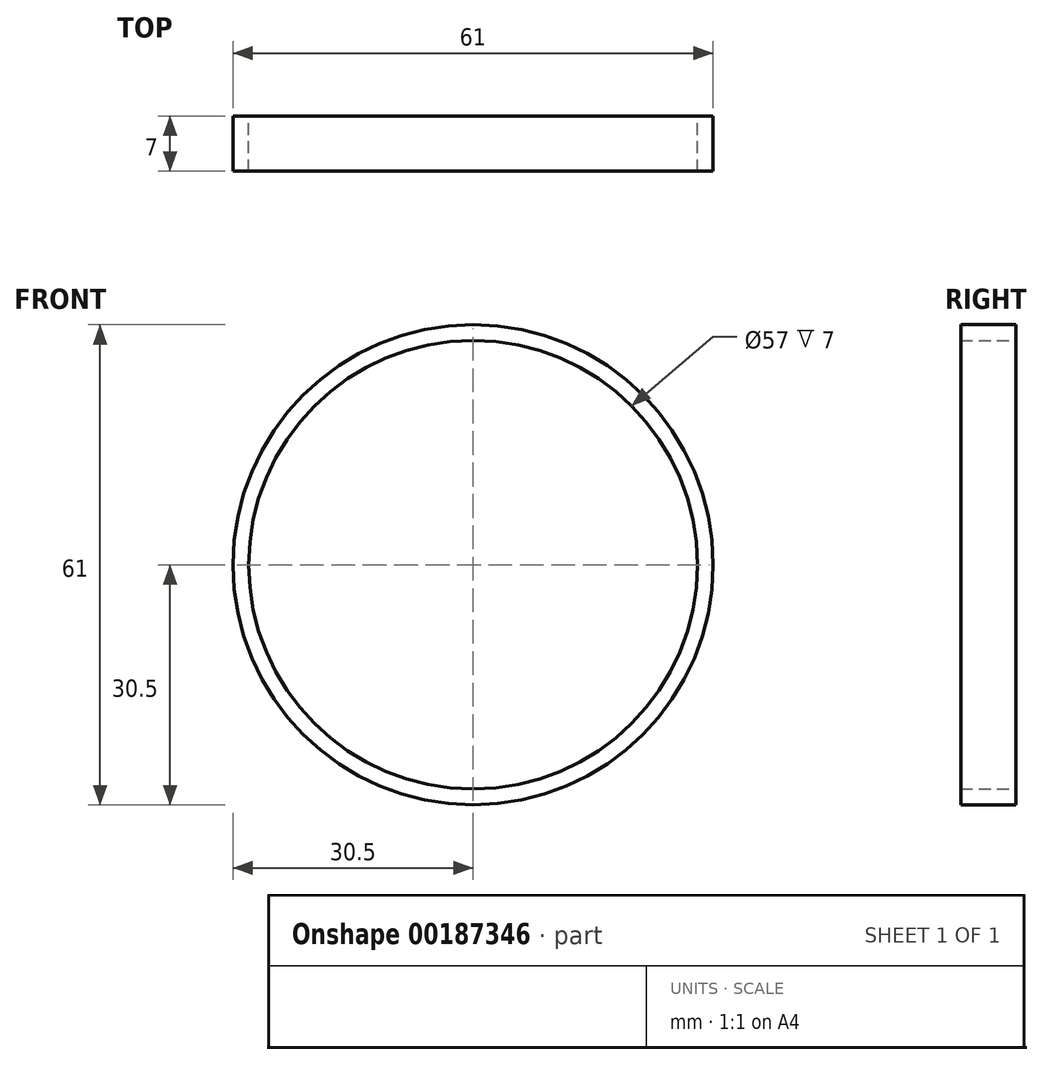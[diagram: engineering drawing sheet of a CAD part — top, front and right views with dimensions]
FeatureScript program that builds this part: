
annotation { "Feature Type Name" : "Feature", "Feature Type Description" : "" }
export const myFeature = defineFeature(function(context is Context, id is Id, definition is map)
    precondition{}
    {
        {
            var Q0;
            Q0=qCreatedBy(makeId("Front.planeOp"),FACE);
            var sketch = newSketch(context, id + "F0", { "sketchPlane" : qUnion([Q0])});
            skCircle(sketch, "E0", {"center": v(0, 0) * mm, "radius": 30.5 * mm});
            skCircle(sketch, "E1", {"center": v(0, 0) * mm, "radius": 28.5 * mm});
            skSolve(sketch);
        }
        {
            var Q0;
            Q0=makeQuery(id+"F0.imprint","IMPRINT",FACE,{"disambiguationData":[TD([[makeQuery(id+"F0.imprint","IMPRINT",EDGE,{"derivedFrom":sQuery(id+"F0.wireOp",EDGE,"E0")}),1.0]])]});
            extrude(context, id + "F1", {"entities" : qUnion([Q0]), "depth" : 7 * mm});
        }
    });
